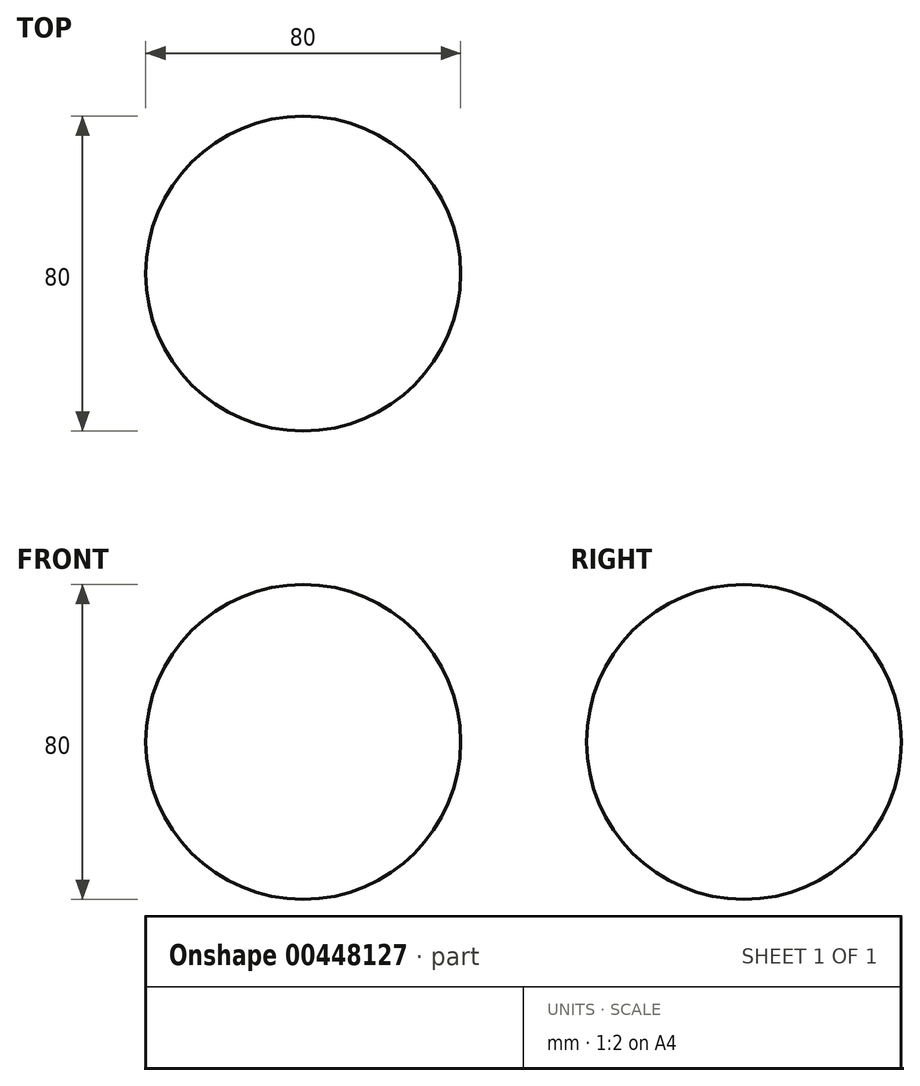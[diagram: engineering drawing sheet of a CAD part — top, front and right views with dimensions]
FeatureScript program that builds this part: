
annotation { "Feature Type Name" : "Feature", "Feature Type Description" : "" }
export const myFeature = defineFeature(function(context is Context, id is Id, definition is map)
    precondition{}
    {
        {
            var Q0;
            Q0=qCreatedBy(makeId("Front.planeOp"),FACE);
            var sketch = newSketch(context, id + "F0", { "sketchPlane" : qUnion([Q0])});
            skArc(sketch, "E0", {"start": v(0, -40) * mm, "mid": v(40, 0) * mm, "end": v(0, 40) * mm});
            skLineSegment(sketch, "E1", {"start": v(0, 0) * mm, "end": v(0, 52.6) * mm, "construction": true});
            skLineSegment(sketch, "E2", {"start": v(0, -40) * mm, "end": v(0, 40) * mm});
            skSolve(sketch);
        }
        {
            var Q0;
            Q0=makeQuery(id+"F0.imprint","IMPRINT",FACE,{"disambiguationData":[TD([[makeQuery(id+"F0.imprint","IMPRINT",EDGE,{"derivedFrom":sQuery(id+"F0.wireOp",EDGE,"E0")}),1.0]])]});
            var Q1;
            Q1=sQuery(id+"F0.wireOp",EDGE,"E1");
            revolve(context, id + "F1", {"entities" : qUnion([Q0]), "axis" : qUnion([Q1]), "revolveType" : RevolveType.FULL});
        }
    });
